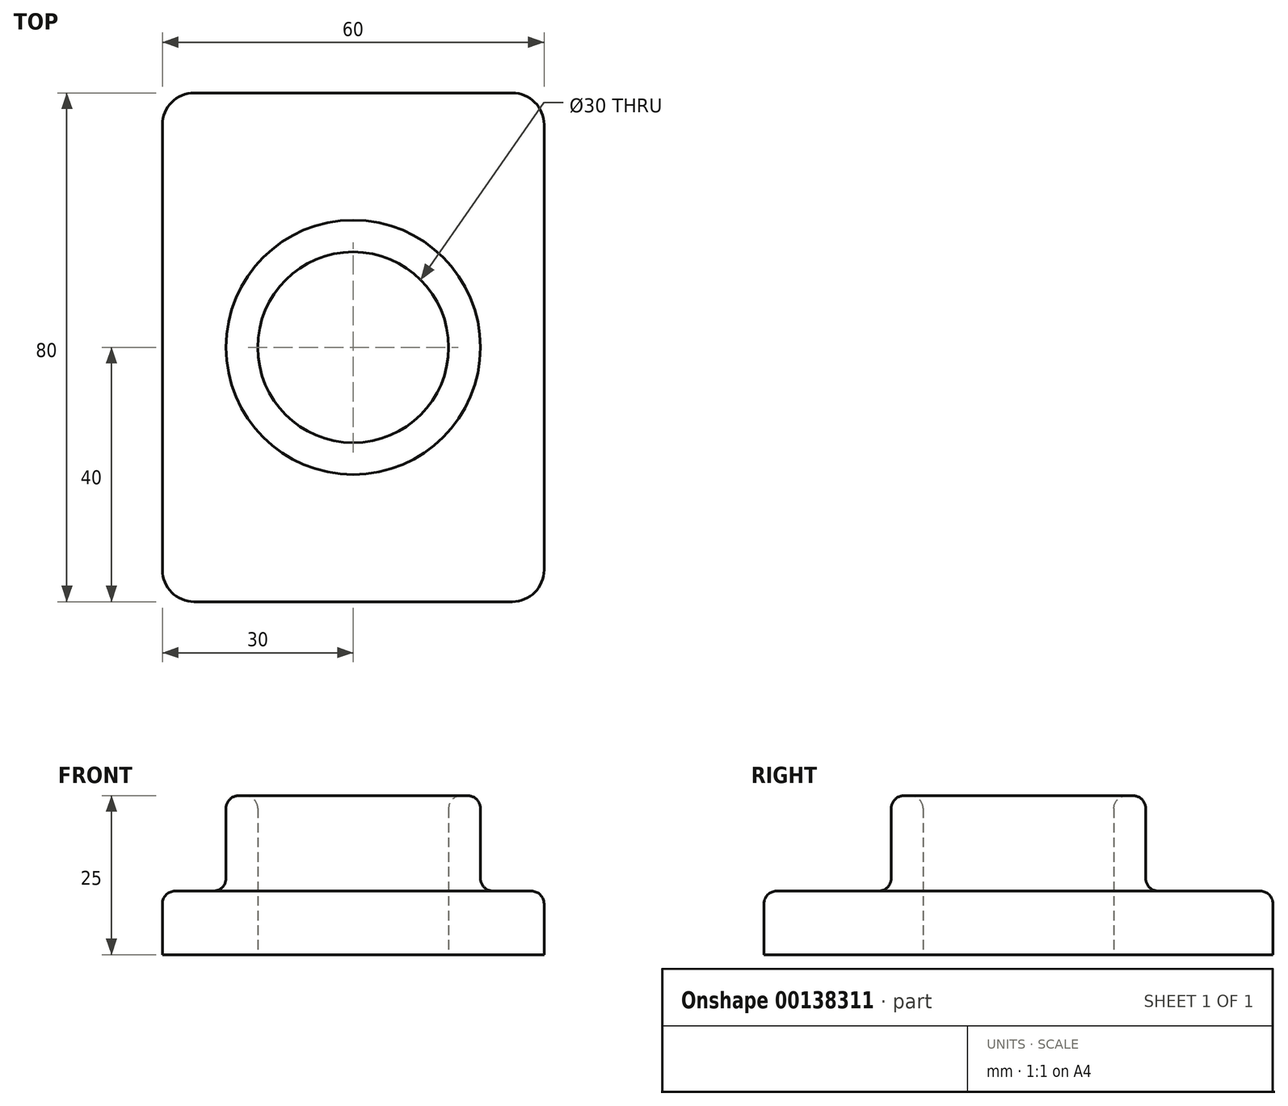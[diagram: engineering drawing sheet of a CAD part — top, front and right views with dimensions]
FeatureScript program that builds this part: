
annotation { "Feature Type Name" : "Feature", "Feature Type Description" : "" }
export const myFeature = defineFeature(function(context is Context, id is Id, definition is map)
    precondition{}
    {
        {
            var Q0;
            Q0=qCreatedBy(makeId("Top.planeOp"),FACE);
            var sketch = newSketch(context, id + "F0", { "sketchPlane" : qUnion([Q0])});
            skLineSegment(sketch, "E0.bottom", {"start": v(25, -40) * mm, "end": v(-25, -40) * mm});
            skLineSegment(sketch, "E0.top", {"start": v(25, 40) * mm, "end": v(-25, 40) * mm});
            skLineSegment(sketch, "E0.left", {"start": v(30, -35) * mm, "end": v(30, 35) * mm});
            skLineSegment(sketch, "E0.right", {"start": v(-30, -35) * mm, "end": v(-30, 35) * mm});
            skPoint(sketch, "E0.middle", {"position": v(0, 0) * mm});
            skCircle(sketch, "E1", {"center": v(0, 0) * mm, "radius": 15 * mm});
            skPoint(sketch, "E2.visualSharp", {"position": v(30, 40) * mm});
            skArc(sketch, "E2.filletArc", {"start": v(30, 35) * mm, "mid": v(28.54, 38.54) * mm, "end": v(25, 40) * mm});
            skPoint(sketch, "E3.visualSharp", {"position": v(-30, 40) * mm});
            skArc(sketch, "E3.filletArc", {"start": v(-25, 40) * mm, "mid": v(-28.54, 38.54) * mm, "end": v(-30, 35) * mm});
            skPoint(sketch, "E4.visualSharp", {"position": v(-30, -40) * mm});
            skArc(sketch, "E4.filletArc", {"start": v(-30, -35) * mm, "mid": v(-28.54, -38.54) * mm, "end": v(-25, -40) * mm});
            skPoint(sketch, "E5.visualSharp", {"position": v(30, -40) * mm});
            skArc(sketch, "E5.filletArc", {"start": v(25, -40) * mm, "mid": v(28.54, -38.54) * mm, "end": v(30, -35) * mm});
            skSolve(sketch);
        }
        {
            var Q0;
            Q0=makeQuery(id+"F0.imprint","IMPRINT",FACE,{"disambiguationData":[TD([[makeQuery(id+"F0.imprint","IMPRINT",EDGE,{"derivedFrom":sQuery(id+"F0.wireOp",EDGE,"E0.bottom")}),-1.0]])]});
            extrude(context, id + "F1", {"entities" : qUnion([Q0]), "depth" : 10 * mm});
        }
        {
            var Q0;
            Q0=makeQuery(id+"F1.opExtrude","CAP_FACE",FACE,{"disambiguationData":[OSD([sQuery(id+"F0.wireOp",EDGE,"E0.bottom"),sQuery(id+"F0.wireOp",EDGE,"E0.top"),sQuery(id+"F0.wireOp",EDGE,"E0.left"),sQuery(id+"F0.wireOp",EDGE,"E0.right"),sQuery(id+"F0.wireOp",EDGE,"E1")])],"isStart":false});
            var sketch = newSketch(context, id + "F2", { "sketchPlane" : qUnion([Q0])});
            skCircle(sketch, "E6.0", {"center": v(0, 0) * mm, "radius": 15 * mm});
            skCircle(sketch, "E7.0", {"center": v(0, 0) * mm, "radius": 20 * mm});
            skSolve(sketch);
        }
        {
            var Q0;
            Q0=makeQuery(id+"F2.imprint","IMPRINT",FACE,{"disambiguationData":[TD([[makeQuery(id+"F2.imprint","IMPRINT",EDGE,{"derivedFrom":sQuery(id+"F2.wireOp",EDGE,"E6.0")}),-1.0]])]});
            extrude(context, id + "F3", {"entities" : qUnion([Q0]), "operationType" : NewBodyOperationType.ADD, "depth" : 15 * mm});
        }
        {
            var Q0;
            Q0=makeQuery(id+"F3.opExtrude","CAP_FACE",FACE,{"disambiguationData":[OSD([sQuery(id+"F2.wireOp",EDGE,"E6.0"),sQuery(id+"F2.wireOp",EDGE,"E7.0")])],"isStart":false});
            var Q1;
            Q1=makeQuery(id+"F1.opExtrude","CAP_FACE",FACE,{"disambiguationData":[OSD([sQuery(id+"F0.wireOp",EDGE,"E0.bottom"),sQuery(id+"F0.wireOp",EDGE,"E0.top"),sQuery(id+"F0.wireOp",EDGE,"E0.left"),sQuery(id+"F0.wireOp",EDGE,"E0.right"),sQuery(id+"F0.wireOp",EDGE,"E1"),sQuery(id+"F0.wireOp",EDGE,"E2.filletArc"),sQuery(id+"F0.wireOp",EDGE,"E3.filletArc"),sQuery(id+"F0.wireOp",EDGE,"E4.filletArc"),sQuery(id+"F0.wireOp",EDGE,"E5.filletArc")])],"isStart":false});
            fillet(context, id + "F4", {"entities" : qUnion([Q0, Q1]), "radius" : 2 * mm, "tangentPropagation" : true, "allowEdgeOverflow" : false});
        }
    });
